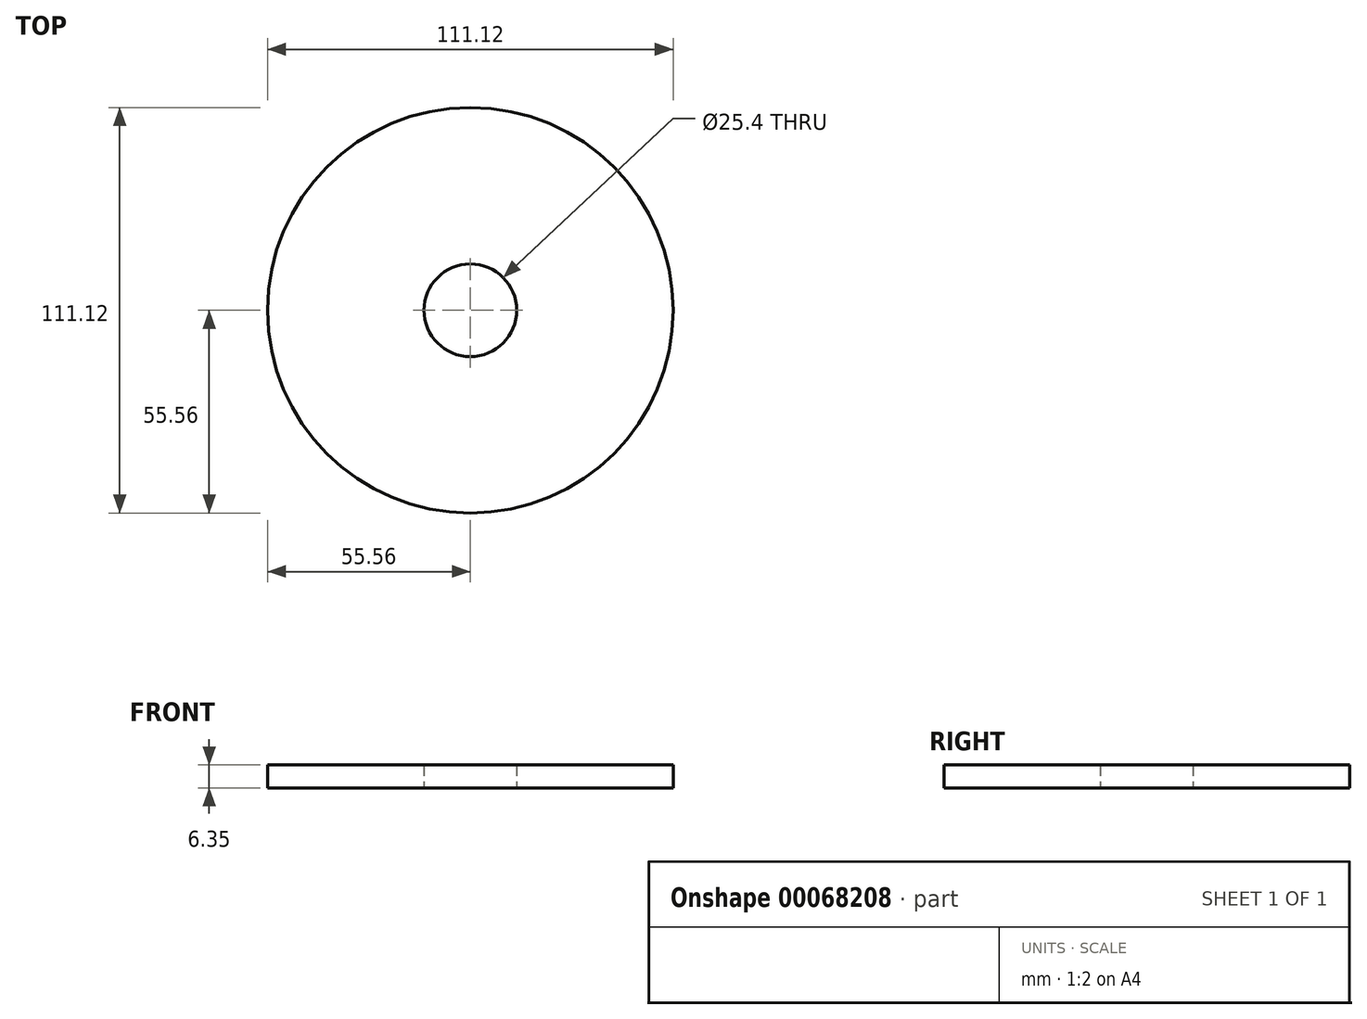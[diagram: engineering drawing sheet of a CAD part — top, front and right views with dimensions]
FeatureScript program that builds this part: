
annotation { "Feature Type Name" : "Feature", "Feature Type Description" : "" }
export const myFeature = defineFeature(function(context is Context, id is Id, definition is map)
    precondition{}
    {
        {
            var Q0;
            Q0=qCreatedBy(makeId("Top.planeOp"),FACE);
            var sketch = newSketch(context, id + "F0", { "sketchPlane" : qUnion([Q0])});
            skCircle(sketch, "E0", {"center": v(0, 0) * mm, "radius": 55.56 * mm});
            skCircle(sketch, "E1", {"center": v(0, 0) * mm, "radius": 12.7 * mm});
            skSolve(sketch);
        }
        {
            var Q0;
            Q0=makeQuery(id+"F0.imprint","IMPRINT",FACE,{"disambiguationData":[TD([[makeQuery(id+"F0.imprint","IMPRINT",EDGE,{"derivedFrom":sQuery(id+"F0.wireOp",EDGE,"E0")}),1.0]])]});
            extrude(context, id + "F1", {"entities" : qUnion([Q0]), "depth" : 6.35 * mm});
        }
    });
